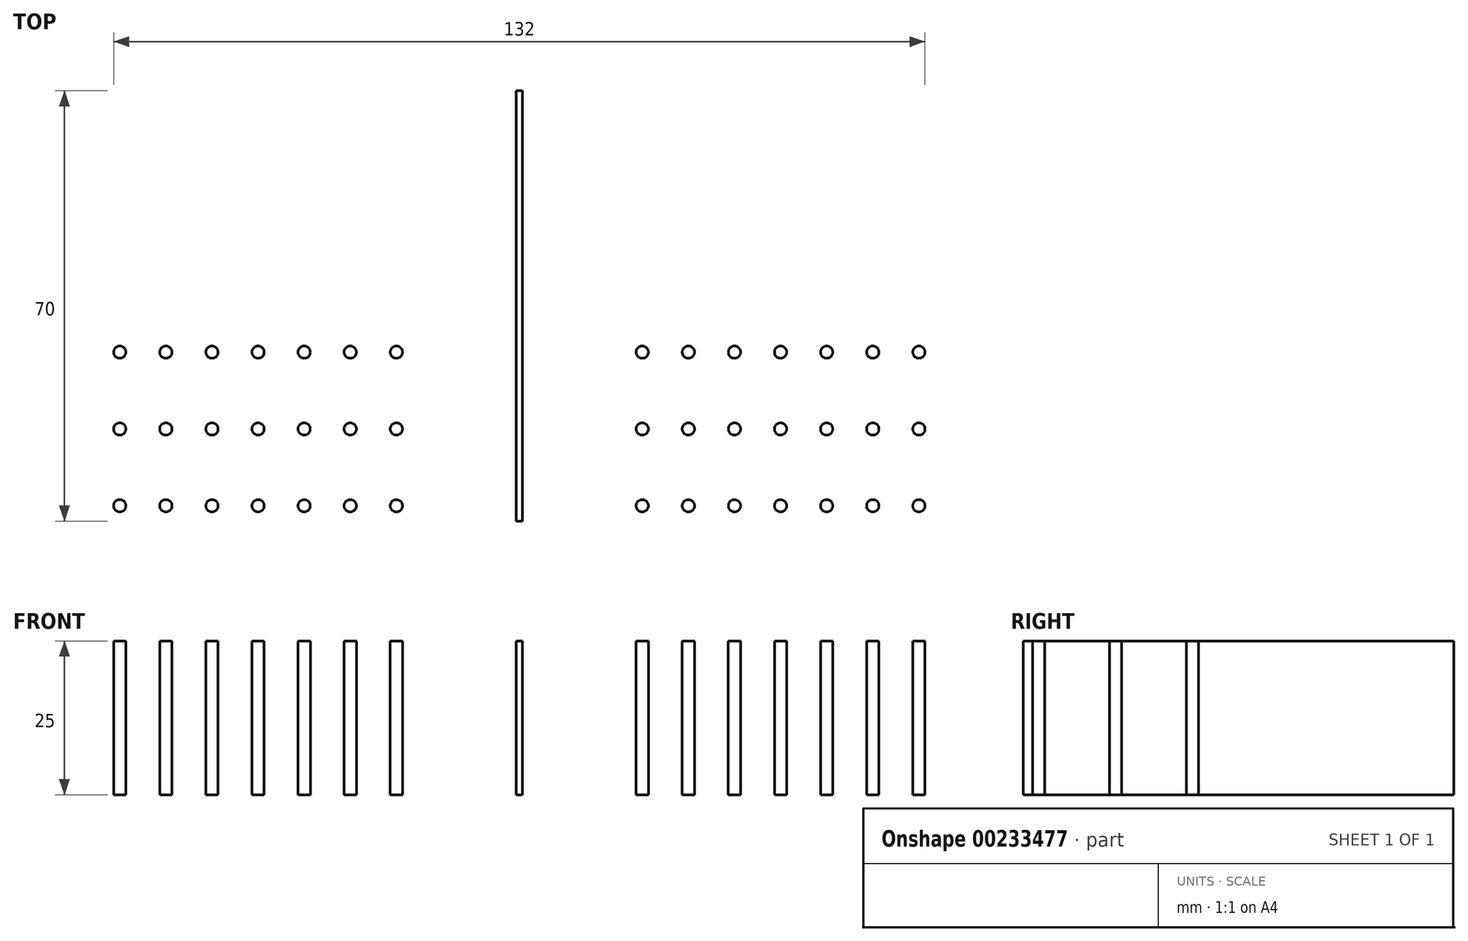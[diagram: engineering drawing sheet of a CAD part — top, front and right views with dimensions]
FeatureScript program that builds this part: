
annotation { "Feature Type Name" : "Feature", "Feature Type Description" : "" }
export const myFeature = defineFeature(function(context is Context, id is Id, definition is map)
    precondition{}
    {
        {
            var Q0;
            Q0=qCreatedBy(makeId("Top.planeOp"),FACE);
            var sketch = newSketch(context, id + "F0", { "sketchPlane" : qUnion([Q0])});
            skLineSegment(sketch, "E0.top", {"start": v(0, 70) * mm, "end": v(-70, 70) * mm});
            skLineSegment(sketch, "E0.left", {"start": v(0, 0) * mm, "end": v(0, 70) * mm});
            skLineSegment(sketch, "E0.right", {"start": v(-70, 0) * mm, "end": v(-70, 70) * mm});
            skPoint(sketch, "E1", {"position": v(46.85, 15) * mm});
            skPoint(sketch, "E2", {"position": v(46.85, 27.5) * mm});
            skCircle(sketch, "E3", {"center": v(46.85, 27.5) * mm, "radius": 1 * mm});
            skCircle(sketch, "E4", {"center": v(46.85, 15) * mm, "radius": 1 * mm});
            skLineSegment(sketch, "E5.bottom", {"start": v(-3.65, 70) * mm, "end": v(-2.65, 70) * mm});
            skLineSegment(sketch, "E5.top", {"start": v(-3.65, 0) * mm, "end": v(-2.65, 0) * mm});
            skLineSegment(sketch, "E5.left", {"start": v(-3.65, 70) * mm, "end": v(-3.65, 0) * mm});
            skLineSegment(sketch, "E5.right", {"start": v(-2.65, 70) * mm, "end": v(-2.65, 0) * mm});
            skLineSegment(sketch, "E6", {"start": v(-3.15, 56.96) * mm, "end": v(-3.15, -7.8) * mm});
            skPoint(sketch, "E7", {"position": v(-38.15, 27.5) * mm});
            skPoint(sketch, "E8", {"position": v(-38.15, 15) * mm});
            skCircle(sketch, "E9", {"center": v(-38.15, 27.5) * mm, "radius": 1 * mm});
            skCircle(sketch, "E10", {"center": v(-38.15, 15) * mm, "radius": 1 * mm});
            skPoint(sketch, "E11", {"position": v(-23.15, 27.5) * mm});
            skPoint(sketch, "E12", {"position": v(-23.15, 15) * mm});
            skCircle(sketch, "E13", {"center": v(-23.15, 27.5) * mm, "radius": 1 * mm});
            skCircle(sketch, "E14", {"center": v(-23.15, 15) * mm, "radius": 1 * mm});
            skCircle(sketch, "E15.MirrorC", {"center": v(31.85, 27.5) * mm, "radius": 1 * mm});
            skCircle(sketch, "E16.MirrorC", {"center": v(16.85, 27.5) * mm, "radius": 1 * mm});
            skCircle(sketch, "E17.MirrorC", {"center": v(31.85, 15) * mm, "radius": 1 * mm});
            skCircle(sketch, "E18.MirrorC", {"center": v(16.85, 15) * mm, "radius": 1 * mm});
            skPoint(sketch, "E19", {"position": v(-68.15, 27.5) * mm});
            skPoint(sketch, "E20", {"position": v(-68.15, 15) * mm});
            skCircle(sketch, "E21", {"center": v(-68.15, 27.5) * mm, "radius": 1 * mm});
            skCircle(sketch, "E22", {"center": v(-68.15, 15) * mm, "radius": 1 * mm});
            skCircle(sketch, "E23.MirrorC", {"center": v(61.85, 27.5) * mm, "radius": 1 * mm});
            skPoint(sketch, "E24.MirrorP", {"position": v(61.85, 15) * mm});
            skCircle(sketch, "E25.MirrorC", {"center": v(61.85, 15) * mm, "radius": 1 * mm});
            skCircle(sketch, "E26.1.0.0", {"center": v(-60.65, 27.5) * mm, "radius": 1 * mm});
            skCircle(sketch, "E26.1.0.1", {"center": v(-60.65, 15) * mm, "radius": 1 * mm});
            skPoint(sketch, "E26.1.0.2", {"position": v(-60.65, 15) * mm});
            skPoint(sketch, "E26.1.0.3", {"position": v(-60.65, 27.5) * mm});
            skCircle(sketch, "E26.2.0.0", {"center": v(-53.15, 27.5) * mm, "radius": 1 * mm});
            skCircle(sketch, "E26.2.0.1", {"center": v(-53.15, 15) * mm, "radius": 1 * mm});
            skPoint(sketch, "E26.2.0.2", {"position": v(-53.15, 15) * mm});
            skPoint(sketch, "E26.2.0.3", {"position": v(-53.15, 27.5) * mm});
            skLineSegment(sketch, "E26.direction1", {"start": v(-68.15, 15) * mm, "end": v(-60.65, 15) * mm, "construction": true});
            skCircle(sketch, "E27.0.3.0", {"center": v(-45.65, 27.5) * mm, "radius": 1 * mm});
            skCircle(sketch, "E27.2.3.0", {"center": v(-45.65, 15) * mm, "radius": 1 * mm});
            skPoint(sketch, "E27.4.3.0", {"position": v(-45.65, 15) * mm});
            skPoint(sketch, "E27.5.3.0", {"position": v(-45.65, 27.5) * mm});
            skPoint(sketch, "E28.MirrorP", {"position": v(54.35, 27.5) * mm});
            skPoint(sketch, "E29.MirrorP", {"position": v(54.35, 15) * mm});
            skCircle(sketch, "E30.MirrorC", {"center": v(54.35, 27.5) * mm, "radius": 1 * mm});
            skCircle(sketch, "E31.MirrorC", {"center": v(54.35, 15) * mm, "radius": 1 * mm});
            skCircle(sketch, "E32.MirrorC", {"center": v(39.35, 27.5) * mm, "radius": 1 * mm});
            skCircle(sketch, "E33.MirrorC", {"center": v(39.35, 15) * mm, "radius": 1 * mm});
            skCircle(sketch, "E34.0.5.0", {"center": v(-30.65, 27.5) * mm, "radius": 1 * mm});
            skCircle(sketch, "E34.2.5.0", {"center": v(-30.65, 15) * mm, "radius": 1 * mm});
            skPoint(sketch, "E34.4.5.0", {"position": v(-30.65, 15) * mm});
            skPoint(sketch, "E34.5.5.0", {"position": v(-30.65, 27.5) * mm});
            skPoint(sketch, "E35.MirrorP", {"position": v(24.35, 27.5) * mm});
            skCircle(sketch, "E36.MirrorC", {"center": v(24.35, 27.5) * mm, "radius": 1 * mm});
            skCircle(sketch, "E37.MirrorC", {"center": v(24.35, 15) * mm, "radius": 1 * mm});
            skLineSegment(sketch, "E38", {"start": v(-68.15, 15) * mm, "end": v(-23.15, 15) * mm, "construction": true});
            skCircle(sketch, "E39.MirrorC", {"center": v(-38.15, 2.5) * mm, "radius": 1 * mm});
            skCircle(sketch, "E40.MirrorC", {"center": v(-68.15, 2.5) * mm, "radius": 1 * mm});
            skPoint(sketch, "E41.MirrorP", {"position": v(-30.65, 2.5) * mm});
            skPoint(sketch, "E42.MirrorP", {"position": v(-45.65, 2.5) * mm});
            skCircle(sketch, "E43.MirrorC", {"center": v(-53.15, 2.5) * mm, "radius": 1 * mm});
            skCircle(sketch, "E44.MirrorC", {"center": v(-30.65, 2.5) * mm, "radius": 1 * mm});
            skPoint(sketch, "E45.MirrorP", {"position": v(-60.65, 2.5) * mm});
            skCircle(sketch, "E46.MirrorC", {"center": v(-23.15, 2.5) * mm, "radius": 1 * mm});
            skCircle(sketch, "E47.MirrorC", {"center": v(-60.65, 2.5) * mm, "radius": 1 * mm});
            skCircle(sketch, "E48.MirrorC", {"center": v(-45.65, 2.5) * mm, "radius": 1 * mm});
            skCircle(sketch, "E49.MirrorC", {"center": v(31.85, 2.5) * mm, "radius": 1 * mm});
            skCircle(sketch, "E50.MirrorC", {"center": v(24.35, 2.5) * mm, "radius": 1 * mm});
            skCircle(sketch, "E51.MirrorC", {"center": v(54.35, 2.5) * mm, "radius": 1 * mm});
            skPoint(sketch, "E52.MirrorP", {"position": v(61.85, 2.5) * mm});
            skCircle(sketch, "E53.MirrorC", {"center": v(16.85, 2.5) * mm, "radius": 1 * mm});
            skPoint(sketch, "E54.MirrorP", {"position": v(39.35, 2.5) * mm});
            skCircle(sketch, "E55.MirrorC", {"center": v(46.85, 2.5) * mm, "radius": 1 * mm});
            skCircle(sketch, "E56.MirrorC", {"center": v(61.85, 2.5) * mm, "radius": 1 * mm});
            skCircle(sketch, "E57.MirrorC", {"center": v(39.35, 2.5) * mm, "radius": 1 * mm});
            skSolve(sketch);
        }
        {
            var Q0;
            Q0=qSketchRegion(id+"F0",true);
            extrude(context, id + "F1", {"entities" : qUnion([Q0]), "depth" : 25 * mm, "offsetDistance" : 25 * mm});
        }
    });
